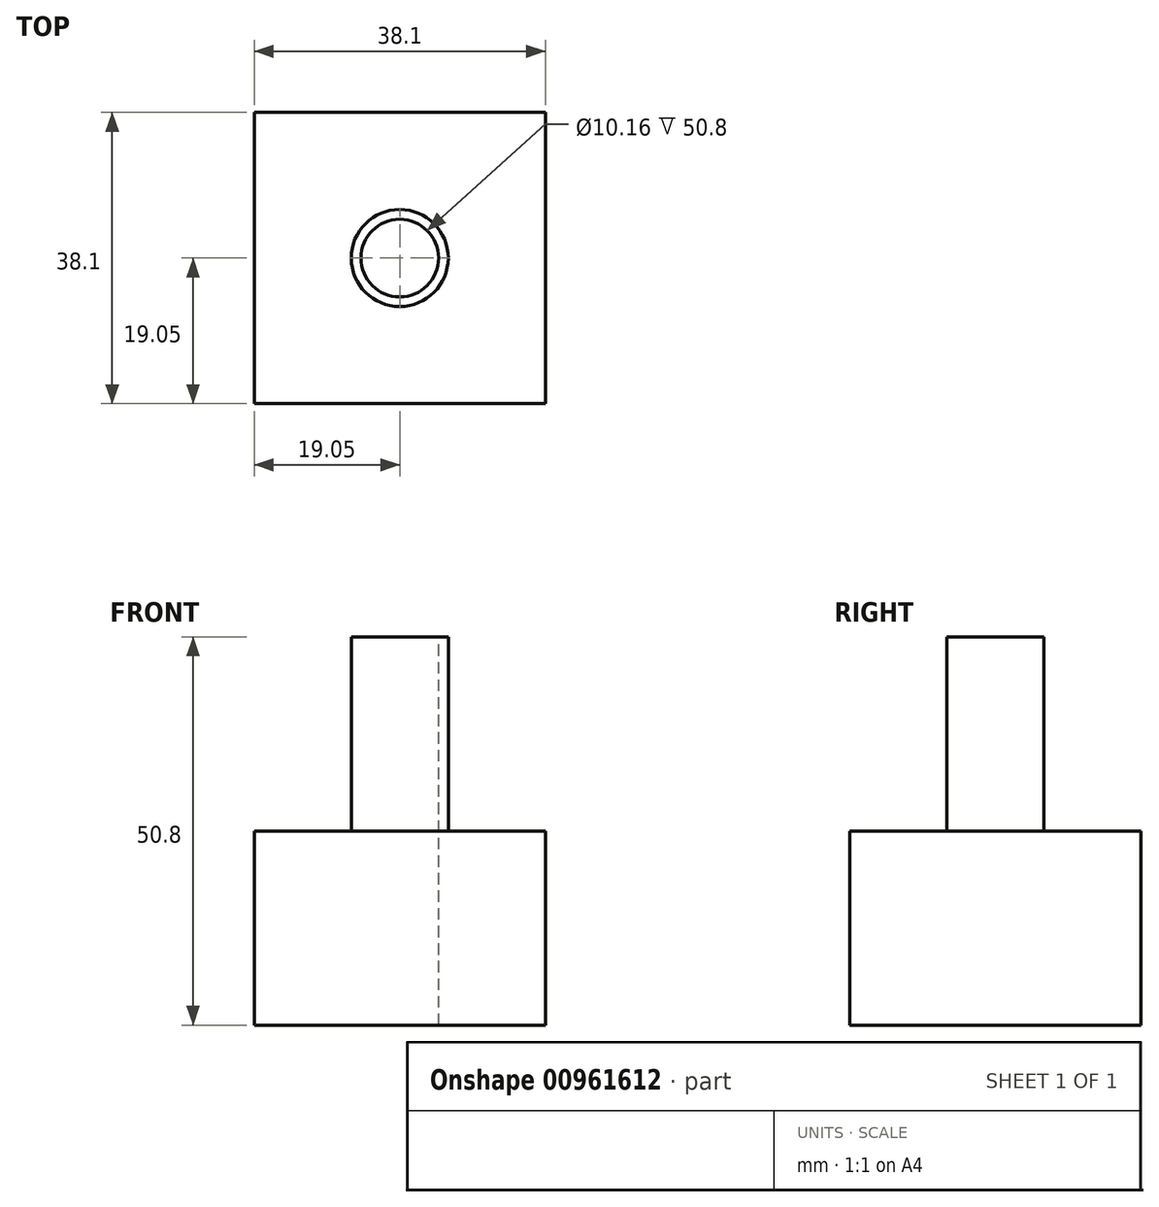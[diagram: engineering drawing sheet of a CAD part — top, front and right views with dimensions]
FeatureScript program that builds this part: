
annotation { "Feature Type Name" : "Feature", "Feature Type Description" : "" }
export const myFeature = defineFeature(function(context is Context, id is Id, definition is map)
    precondition{}
    {
        {
            var Q0;
            Q0=qCreatedBy(makeId("Top.planeOp"),FACE);
            var sketch = newSketch(context, id + "F0", { "sketchPlane" : qUnion([Q0])});
            skLineSegment(sketch, "E0.bottom", {"start": v(0, 0) * mm, "end": v(38.1, 0) * mm});
            skLineSegment(sketch, "E0.top", {"start": v(0, 38.1) * mm, "end": v(38.1, 38.1) * mm});
            skLineSegment(sketch, "E0.left", {"start": v(0, 0) * mm, "end": v(0, 38.1) * mm});
            skLineSegment(sketch, "E0.right", {"start": v(38.1, 0) * mm, "end": v(38.1, 38.1) * mm});
            skSolve(sketch);
        }
        {
            var Q0;
            Q0=makeQuery(id+"F0.imprint","IMPRINT",FACE,{"disambiguationData":[TD([[makeQuery(id+"F0.imprint","IMPRINT",EDGE,{"derivedFrom":sQuery(id+"F0.wireOp",EDGE,"E0.bottom")}),1.0]])]});
            extrude(context, id + "F1", {"entities" : qUnion([Q0]), "depth" : 25.4 * mm, "offsetDistance" : 25.4 * mm});
        }
        {
            var Q0;
            Q0=makeQuery(id+"F1.opExtrude","CAP_FACE",FACE,{"disambiguationData":[OSD([sQuery(id+"F0.wireOp",EDGE,"E0.bottom"),sQuery(id+"F0.wireOp",EDGE,"E0.top"),sQuery(id+"F0.wireOp",EDGE,"E0.left"),sQuery(id+"F0.wireOp",EDGE,"E0.right")])],"isStart":false});
            cPlane(context, id + "F2", {"entities" : qUnion([Q0]), "cplaneType" : CPlaneType.OFFSET, "offset" : 0 * mm, "width" : 152.4 * mm, "height" : 152.4 * mm});
        }
        {
            var Q0;
            Q0=qCreatedBy(id+"F2.planeOp",FACE);
            var sketch = newSketch(context, id + "F3", { "sketchPlane" : qUnion([Q0])});
            skPoint(sketch, "E1.endSnap0", {"position": v(19.05, 19.05) * mm});
            skCircle(sketch, "E2", {"center": v(19.05, 19.05) * mm, "radius": 6.35 * mm});
            skSolve(sketch);
        }
        {
            var Q0;
            Q0=makeQuery(id+"F3.imprint","IMPRINT",FACE,{"disambiguationData":[TD([[makeQuery(id+"F3.imprint","IMPRINT",EDGE,{"derivedFrom":sQuery(id+"F3.wireOp",EDGE,"E2")}),1.0]])]});
            extrude(context, id + "F4", {"entities" : qUnion([Q0]), "operationType" : NewBodyOperationType.ADD, "depth" : 25.4 * mm, "offsetDistance" : 25.4 * mm});
        }
        {
            var Q0;
            Q0=makeQuery(id+"F4.opExtrude","CAP_FACE",FACE,{"disambiguationData":[OSD([sQuery(id+"F3.wireOp",EDGE,"E2")])],"isStart":false});
            cPlane(context, id + "F5", {"entities" : qUnion([Q0]), "cplaneType" : CPlaneType.OFFSET, "offset" : 0 * mm, "width" : 152.4 * mm, "height" : 152.4 * mm});
        }
        {
            var Q0;
            Q0=qCreatedBy(id+"F5.planeOp",FACE);
            var sketch = newSketch(context, id + "F6", { "sketchPlane" : qUnion([Q0])});
            skCircle(sketch, "E3", {"center": v(19.05, 19.05) * mm, "radius": 5.08 * mm});
            skSolve(sketch);
        }
        {
            var Q0;
            Q0=sQuery(id+"F6.wireOp",VERTEX,"E3.center");
            var Q1;
            Q1=makeQuery(id+"F1.opExtrude","SWEPT_BODY",BODY,{"disambiguationData":[OSD([sQuery(id+"F0.wireOp",EDGE,"E0.bottom"),sQuery(id+"F0.wireOp",EDGE,"E0.top"),sQuery(id+"F0.wireOp",EDGE,"E0.left"),sQuery(id+"F0.wireOp",EDGE,"E0.right")])]});
            hole(context, id + "F7", {"style" : HoleStyle.SIMPLE, "endStyle" : HoleEndStyle.THROUGH, "holeDiameter" : 10.16 * mm, "majorDiameter" : 6.35 * mm, "isTappedThrough" : true, "tappedDepth" : 12.7 * mm, "tapClearance" : 3, "locations" : qUnion([Q0]), "scope" : qUnion([Q1])});
        }
    });
